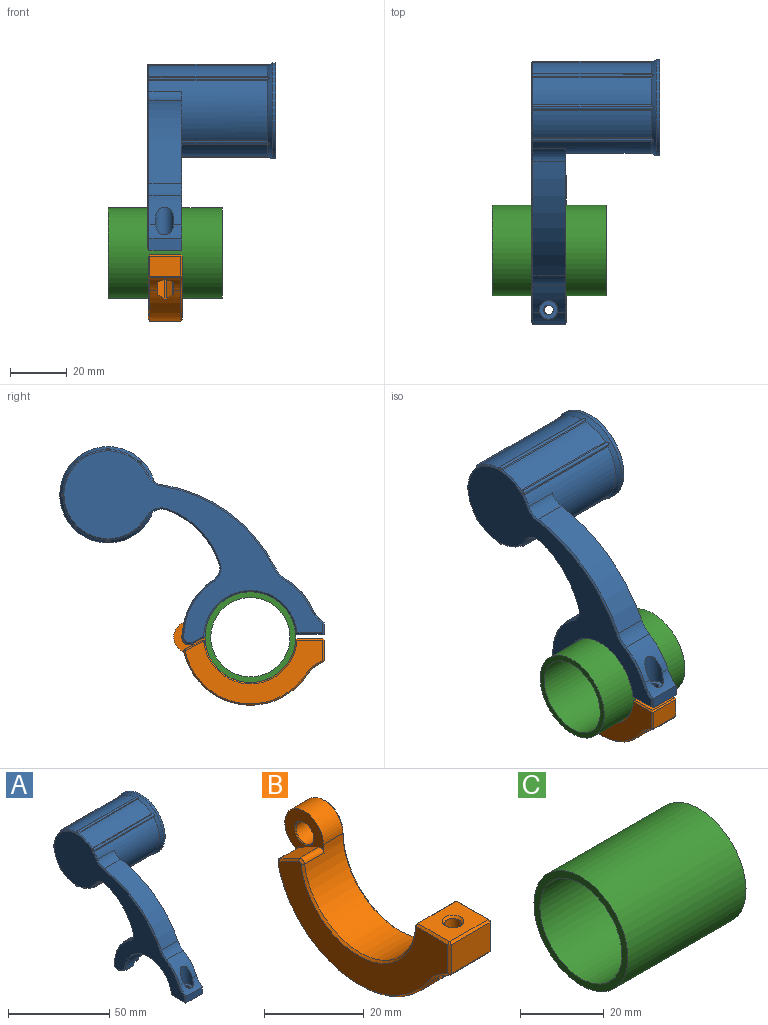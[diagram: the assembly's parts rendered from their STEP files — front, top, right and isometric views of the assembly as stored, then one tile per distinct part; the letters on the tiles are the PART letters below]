
ASSEMBLY  parts=3 mates=3
PART A: 98 faces, bbox 45x92.8x69.4 mm
  f0: cone r=15.9mm half-angle=30deg, axis (1,0,0), area 198.8mm2, adj f1,f2,f3,f4,f5,f6,f11,f26
  f1: cylinder r=15.9mm len=41.5mm, axis (-1,0,0), area 776.9mm2, adj f0,f20,f39,f40,f41,f54,f67,f97
  f2: cylinder r=15.9mm len=41.5mm, axis (-1,0,0), area 438.1mm2, adj f0,f42,f43,f90
  f3: cylinder r=15.9mm len=41.5mm, axis (-1,0,0), area 438.1mm2, adj f0,f44,f45,f82
  f4: cylinder r=15.9mm len=41.5mm, axis (-1,0,0), area 438.1mm2, adj f0,f46,f47,f74
  f5: cylinder r=15.9mm len=41.5mm, axis (-1,0,0), area 438.1mm2, adj f0,f48,f49,f66
  f6: cylinder r=15.9mm len=41.5mm, axis (-1,0,0), area 438.1mm2, adj f0,f50,f51,f58
  f7: cylinder r=23.9mm len=20.02mm, axis (-1,0,0), area 230.5mm2, adj f19,f20,f24,f36,f37,f89
  f8: cylinder r=15.9mm len=31.77mm, axis (-1,0,0), area 538mm2, adj f9,f18,f20,f24,f38,f83
  f9: plane 5.5x4.36mm, normal (0,-0.45,-0.89), area 26.9mm2, adj f8,f19,f24,f85
  f10: plane 5x5mm, normal (1,0,0), area 19.6mm2, adj f19
  f11: cylinder r=15.9mm len=41.5mm, axis (-1,0,0), area 438.1mm2, adj f0,f52,f53,f59
  f12: plane 91.27x67.9mm, normal (-1,0,0), area 1714.1mm2, adj f55,f56,f57,f58,f59,f60,f61,f62
  f13: cylinder r=30mm len=18.73mm, axis (-1,0,0), area 309mm2, adj f20,f36,f39,f93
  f14: cylinder r=54mm len=39.91mm, axis (-1,0,0), area 590.2mm2, adj f20,f35,f40,f71
  f15: cylinder r=23.9mm len=11.5mm, axis (-1,0,0), area 122.1mm2, adj f16,f20,f22,f35,f75
  f16: cylinder r=12mm len=11.5mm, axis (-1,0,0), area 54.5mm2, adj f15,f17,f20,f22,f77
  f17: plane 11.5x4mm, normal (0,-1,0), area 46mm2, adj f16,f18,f20,f79
  f18: plane 11.5x10mm, normal (0,0,-1), area 105.9mm2, adj f8,f17,f20,f21,f81
  f19: cylinder r=2.5mm len=11.5mm, axis (-1,0,0), area 122.3mm2, adj f7,f9,f10,f24,f87
  f20: plane 62.17x55.9mm, normal (1,0,0), area 1017.2mm2, adj f1,f7,f8,f13,f14,f15,f16,f17
  f21: cylinder r=1.7mm len=4mm, axis (0,0,-1), area 42.7mm2, adj f18,f23
  f22: cylinder r=3.25mm len=11.15mm, axis (0,0,-1), area 130.2mm2, adj f15,f16,f23
  f23: plane 6.5x6.5mm, normal (0,0,1), area 24.1mm2, adj f21,f22
  f24: plane 9.2x8.54mm, normal (1,0,0), area 32.8mm2, adj f7,f8,f9,f19,f25,f37,f38
  f25: cylinder r=5.7mm len=6mm, axis (1,0,0), area 32mm2, adj f20,f24,f37,f38
  f26: cylinder r=16.9mm len=33.8mm, axis (1,0,0), area 134.6mm2, adj f0,f27
  f27: plane 33.8x33.8mm, normal (1,0,0), area 897.3mm2, adj f26
  f28: cylinder r=0.7mm len=42.37mm, axis (-1,0,0), area 57.8mm2, adj f0,f53,f54,f63
  f29: cylinder r=0.7mm len=42.37mm, axis (-1,0,0), area 57.8mm2, adj f0,f51,f52,f55
  f30: cylinder r=0.7mm len=42.37mm, axis (-1,0,0), area 57.8mm2, adj f0,f49,f50,f62
  f31: cylinder r=0.7mm len=42.37mm, axis (-1,0,0), area 57.8mm2, adj f0,f47,f48,f70
  f32: cylinder r=0.7mm len=42.37mm, axis (-1,0,0), area 57.8mm2, adj f0,f45,f46,f78
  f33: cylinder r=0.7mm len=42.37mm, axis (-1,0,0), area 57.8mm2, adj f0,f43,f44,f86
  f34: cylinder r=0.7mm len=42.37mm, axis (-1,0,0), area 57.8mm2, adj f0,f41,f42,f94
  f35: cylinder r=10mm len=11.5mm, axis (1,0,0), area 64.1mm2, adj f14,f15,f20,f73
  f36: cylinder r=5mm len=11.5mm, axis (-1,0,0), area 75.4mm2, adj f7,f13,f20,f91
  f37: cylinder r=1mm len=6mm, axis (-1,0,0), area 11.7mm2, adj f7,f20,f24,f25
  f38: cylinder r=1mm len=6mm, axis (1,0,0), area 13mm2, adj f8,f20,f24,f25
  f39: cylinder r=6mm len=11.5mm, axis (-1,0,0), area 96.3mm2, adj f1,f13,f20,f95
  f40: cylinder r=6mm len=11.5mm, axis (1,0,0), area 66.7mm2, adj f1,f14,f20,f69
  f41: cylinder r=0.5mm len=41.85mm, axis (1,0,0), area 19.1mm2, adj f0,f1,f34,f96
  f42: cylinder r=0.5mm len=41.85mm, axis (1,0,0), area 19.1mm2, adj f0,f2,f34,f92
  f43: cylinder r=0.5mm len=41.85mm, axis (1,0,0), area 19.1mm2, adj f0,f2,f33,f88
  f44: cylinder r=0.5mm len=41.85mm, axis (1,0,0), area 19.1mm2, adj f0,f3,f33,f84
  f45: cylinder r=0.5mm len=41.85mm, axis (1,0,0), area 19.1mm2, adj f0,f3,f32,f80
  f46: cylinder r=0.5mm len=41.85mm, axis (1,0,0), area 19.1mm2, adj f0,f4,f32,f76
  f47: cylinder r=0.5mm len=41.85mm, axis (1,0,0), area 19.1mm2, adj f0,f4,f31,f72
  f48: cylinder r=0.5mm len=41.85mm, axis (1,0,0), area 19.1mm2, adj f0,f5,f31,f68
  f49: cylinder r=0.5mm len=41.85mm, axis (1,0,0), area 19.1mm2, adj f0,f5,f30,f64
  f50: cylinder r=0.5mm len=41.85mm, axis (1,0,0), area 19.1mm2, adj f0,f6,f30,f60
  f51: cylinder r=0.5mm len=41.85mm, axis (1,0,0), area 19.1mm2, adj f0,f6,f29,f56
  f52: cylinder r=0.5mm len=41.85mm, axis (1,0,0), area 19.1mm2, adj f0,f11,f29,f57
  f53: cylinder r=0.5mm len=41.85mm, axis (1,0,0), area 19.1mm2, adj f0,f11,f28,f61
  f54: cylinder r=0.5mm len=41.85mm, axis (1,0,0), area 19.1mm2, adj f0,f1,f28,f65
  f55: cone r=0.2mm half-angle=45deg, axis (1,0,0), area 0.6mm2, adj f12,f29,f56,f57
  f56: cone r=1mm half-angle=45deg, axis (-1,0,0), area 0.5mm2, adj f12,f51,f55,f58
  f57: cone r=1mm half-angle=45deg, axis (-1,0,0), area 0.5mm2, adj f12,f52,f55,f59
  f58: cone r=15.9mm half-angle=45deg, axis (1,0,0), area 7.3mm2, adj f6,f12,f56,f60
  f59: cone r=15.9mm half-angle=45deg, axis (1,0,0), area 7.3mm2, adj f11,f12,f57,f61
  f60: cone r=1mm half-angle=45deg, axis (-1,0,0), area 0.5mm2, adj f12,f50,f58,f62
  f61: cone r=1mm half-angle=45deg, axis (-1,0,0), area 0.5mm2, adj f12,f53,f59,f63
  f62: cone r=0.2mm half-angle=45deg, axis (1,0,0), area 0.6mm2, adj f12,f30,f60,f64
  f63: cone r=0.2mm half-angle=45deg, axis (1,0,0), area 0.6mm2, adj f12,f28,f61,f65
  f64: cone r=1mm half-angle=45deg, axis (-1,0,0), area 0.5mm2, adj f12,f49,f62,f66
  f65: cone r=1mm half-angle=45deg, axis (-1,0,0), area 0.5mm2, adj f12,f54,f63,f67
  f66: cone r=15.9mm half-angle=45deg, axis (1,0,0), area 7.3mm2, adj f5,f12,f64,f68
  f67: cone r=15.9mm half-angle=45deg, axis (1,0,0), area 3.1mm2, adj f1,f12,f65,f69
  f68: cone r=1mm half-angle=45deg, axis (-1,0,0), area 0.5mm2, adj f12,f48,f66,f70
  f69: cone r=6.5mm half-angle=45deg, axis (-1,0,0), area 4.3mm2, adj f12,f40,f67,f71
  f70: cone r=0.2mm half-angle=45deg, axis (1,0,0), area 0.6mm2, adj f12,f31,f68,f72
  f71: cone r=54mm half-angle=45deg, axis (1,0,0), area 36.1mm2, adj f12,f14,f69,f73
  f72: cone r=1mm half-angle=45deg, axis (-1,0,0), area 0.5mm2, adj f12,f47,f70,f74
  f73: cone r=10.5mm half-angle=45deg, axis (-1,0,0), area 4mm2, adj f12,f35,f71,f75
  f74: cone r=15.9mm half-angle=45deg, axis (1,0,0), area 7.3mm2, adj f4,f12,f72,f76
  f75: cone r=23.9mm half-angle=45deg, axis (1,0,0), area 10mm2, adj f12,f15,f73,f77
  f76: cone r=1mm half-angle=45deg, axis (-1,0,0), area 0.5mm2, adj f12,f46,f74,f78
  f77: cone r=12.5mm half-angle=45deg, axis (-1,0,0), area 4.6mm2, adj f12,f16,f75,f79
  f78: cone r=0.2mm half-angle=45deg, axis (1,0,0), area 0.6mm2, adj f12,f32,f76,f80
  f79: plane 4x0.5mm, normal (-0.71,-0.71,0), area 2.6mm2, adj f12,f17,f77,f81
  f80: cone r=1mm half-angle=45deg, axis (-1,0,0), area 0.5mm2, adj f12,f45,f78,f82
  f81: plane 10.01x0.51mm, normal (-0.71,0,-0.71), area 6.7mm2, adj f12,f18,f79,f83
  f82: cone r=15.9mm half-angle=45deg, axis (1,0,0), area 7.3mm2, adj f3,f12,f80,f84
  f83: cone r=16.4mm half-angle=45deg, axis (-1,0,0), area 34.9mm2, adj f8,f12,f81,f85
  f84: cone r=1mm half-angle=45deg, axis (-1,0,0), area 0.5mm2, adj f12,f44,f82,f86
  f85: plane 4.59x2.54mm, normal (-0.71,-0.32,-0.63), area 3.4mm2, adj f9,f12,f83,f87
  f86: cone r=0.2mm half-angle=45deg, axis (1,0,0), area 0.6mm2, adj f12,f33,f84,f88
  f87: cone r=2.5mm half-angle=45deg, axis (1,0,0), area 3.2mm2, adj f12,f19,f85,f89
  f88: cone r=1mm half-angle=45deg, axis (-1,0,0), area 0.5mm2, adj f12,f43,f86,f90
  f89: cone r=23.9mm half-angle=45deg, axis (1,0,0), area 16.6mm2, adj f7,f12,f87,f91
  f90: cone r=15.9mm half-angle=45deg, axis (1,0,0), area 7.3mm2, adj f2,f12,f88,f92
  f91: cone r=5.5mm half-angle=45deg, axis (-1,0,0), area 4.9mm2, adj f12,f36,f89,f93
  f92: cone r=1mm half-angle=45deg, axis (-1,0,0), area 0.5mm2, adj f12,f42,f90,f94
  f93: cone r=30.5mm half-angle=45deg, axis (-1,0,0), area 19.2mm2, adj f12,f13,f91,f95
  f94: cone r=0.2mm half-angle=45deg, axis (1,0,0), area 0.6mm2, adj f12,f34,f92,f96
  f95: cone r=6.5mm half-angle=45deg, axis (-1,0,0), area 6.2mm2, adj f12,f39,f93,f97
  f96: cone r=1mm half-angle=45deg, axis (-1,0,0), area 0.5mm2, adj f12,f41,f94,f97
  f97: cone r=15.9mm half-angle=45deg, axis (1,0,0), area 2.1mm2, adj f1,f12,f95,f96
PART B: 54 faces, bbox 12.1x52.9x29.5 mm
  f0: cylinder r=15.9mm len=31.77mm, axis (-1,0,0), area 527.7mm2, adj f6,f17,f20,f21,f23,f24
  f1: plane 48.24x22.4mm, normal (-1,0,0), area 431.8mm2, adj f22,f23,f27,f31,f32,f36,f40,f41
  f2: plane 11x9.02mm, normal (0,0,1), area 84mm2, adj f24,f29,f32,f33,f45
  f3: plane 11x7.15mm, normal (0,-1,0), area 78.7mm2, adj f33,f38,f41,f44
  f4: cylinder r=12mm len=11mm, axis (-1,0,0), area 52.6mm2, adj f5,f11,f12,f13,f14,f39,f40,f44
  f5: cylinder r=23.9mm len=43.26mm, axis (-1,0,0), area 599.4mm2, adj f4,f9,f10,f12,f13,f19,f35,f36
  f6: cylinder r=5.5mm len=11mm, axis (-1,0,0), area 131.7mm2, adj f0,f17,f19,f26
  f7: cylinder r=2.52mm len=5.3mm, axis (-1,0,0), area 84.1mm2, adj f46,f47
  f8: plane 51.79x28.4mm, normal (1,0,0), area 474.7mm2, adj f21,f26,f29,f30,f35,f38,f39,f46
  f9: plane 10.64x2.47mm, normal (-0.5,-0.87,0), area 27.1mm2, adj f5,f15,f49,f50
  f10: plane 10.64x2.47mm, normal (0.5,-0.87,0), area 27.1mm2, adj f5,f15,f50,f51
  f11: plane 4.78x2.45mm, normal (-0.5,0.87,0), area 11.8mm2, adj f4,f15,f48,f53
  f12: plane 8.31x2.77mm, normal (-1,0,0), area 18.1mm2, adj f4,f5,f15,f48,f49
  f13: plane 8.31x2.77mm, normal (1,0,0), area 18.1mm2, adj f4,f5,f15,f51,f52
  f14: plane 4.78x2.45mm, normal (0.5,0.87,0), area 11.8mm2, adj f4,f15,f52,f53
  f15: plane 6.54x5.8mm, normal (0,0,-1), area 20mm2, adj f9,f10,f11,f12,f13,f14,f16,f48
  f16: cylinder r=1.7mm len=4.5mm, axis (0,0,-1), area 48.1mm2, adj f15,f45
  f17: plane 11.13x10.65mm, normal (-1,0,0), area 56.6mm2, adj f0,f6,f18,f19,f20,f47
  f18: plane 5.58x5.5mm, normal (0,0.46,0.89), area 34.5mm2, adj f17,f19,f20,f27
  f19: cylinder r=1mm len=11mm, axis (-1,0,0), area 7.7mm2, adj f5,f6,f17,f18,f30,f31
  f20: cylinder r=1mm len=5.5mm, axis (-1,0,0), area 10.6mm2, adj f0,f17,f18,f22
  f21: cone r=15.9mm half-angle=45deg, axis (1,0,0), area 35.2mm2, adj f0,f8,f25,f26
  f22: cone r=0.5mm half-angle=45deg, axis (1,0,0), area 1mm2, adj f1,f20,f23,f27
  f23: cone r=16.4mm half-angle=45deg, axis (-1,0,0), area 33.7mm2, adj f0,f1,f22,f28
  f24: plane 11x0.5mm, normal (0,0.69,0.73), area 7.5mm2, adj f0,f2,f25,f28
  f25: plane 0.5x0.5mm, normal (0.59,0.55,0.59), area 0.2mm2, adj f21,f24,f29
  f26: cone r=5mm half-angle=45deg, axis (-1,0,0), area 16.3mm2, adj f6,f8,f21,f30
  f27: plane 5.81x3.33mm, normal (-0.71,0.32,0.63), area 4.4mm2, adj f1,f18,f22,f31
  f28: plane 0.5x0.5mm, normal (-0.59,0.55,0.59), area 0.2mm2, adj f23,f24,f32
  f29: plane 9.02x0.5mm, normal (0.71,0,0.71), area 6.4mm2, adj f2,f8,f25,f34
  f30: cone r=0.5mm half-angle=45deg, axis (-1,0,0), area 0.2mm2, adj f8,f19,f26,f35
  f31: cone r=0.5mm half-angle=45deg, axis (1,0,0), area 0.7mm2, adj f1,f19,f27,f36
  f32: plane 9.02x0.5mm, normal (-0.71,0,0.71), area 6.4mm2, adj f1,f2,f28,f37
  f33: plane 11x0.5mm, normal (0,-0.71,0.71), area 7.8mm2, adj f2,f3,f34,f37
  f34: plane 0.5x0.5mm, normal (0.58,-0.58,0.58), area 0.2mm2, adj f29,f33,f38
  f35: cone r=23.4mm half-angle=45deg, axis (-1,0,0), area 39.1mm2, adj f5,f8,f30,f39
  f36: cone r=23.9mm half-angle=45deg, axis (1,0,0), area 39.1mm2, adj f1,f5,f31,f40
  f37: plane 0.5x0.5mm, normal (-0.58,-0.58,0.58), area 0.2mm2, adj f32,f33,f41
  f38: plane 7.15x0.5mm, normal (0.71,-0.71,0), area 5.1mm2, adj f3,f8,f34,f42
  f39: cone r=12mm half-angle=45deg, axis (1,0,0), area 5.3mm2, adj f4,f8,f35,f42
  f40: cone r=12.5mm half-angle=45deg, axis (-1,0,0), area 5.3mm2, adj f1,f4,f36,f43
  f41: plane 7.15x0.5mm, normal (-0.71,-0.71,0), area 5.1mm2, adj f1,f3,f37,f43
  f42: plane 0.5x0.5mm, normal (0.64,-0.64,-0.43), area 0.2mm2, adj f38,f39,f44
  f43: plane 0.5x0.5mm, normal (-0.64,-0.64,-0.43), area 0.2mm2, adj f40,f41,f44
  f44: plane 11x0.47mm, normal (0,-0.83,-0.56), area 6.2mm2, adj f3,f4,f42,f43
  f45: cone r=1.7mm half-angle=45deg, axis (0,0,1), area 8.7mm2, adj f2,f16
  f46: cone r=2.52mm half-angle=45deg, axis (1,0,0), area 12.3mm2, adj f7,f8
  f47: cone r=2.73mm half-angle=45deg, axis (-1,0,0), area 4.7mm2, adj f7,f17
  f48: cylinder r=0.5mm len=5.07mm, axis (0,0,-1), area 2.6mm2, adj f4,f11,f12,f15
  f49: cylinder r=0.5mm len=8.9mm, axis (0,0,-1), area 4.5mm2, adj f5,f9,f12,f15
  f50: cylinder r=0.5mm len=10.65mm, axis (0,0,-1), area 5.6mm2, adj f5,f9,f10,f15
  f51: cylinder r=0.5mm len=8.9mm, axis (0,0,-1), area 4.5mm2, adj f5,f10,f13,f15
  f52: cylinder r=0.5mm len=5.07mm, axis (0,0,-1), area 2.6mm2, adj f4,f13,f14,f15
  f53: cylinder r=0.5mm len=3.82mm, axis (0,0,-1), area 2mm2, adj f4,f11,f14,f15
PART C: 4 faces, bbox 40x31.8x31.8 mm
  f0: cylinder r=13.9mm len=40mm, axis (-1,0,0), area 3493.5mm2, adj f2,f3
  f1: cylinder r=15.9mm len=40mm, axis (-1,0,0), area 3996.1mm2, adj f2,f3
  f2: plane 31.8x31.8mm, normal (1,0,0), area 187.2mm2, adj f0,f1
  f3: plane 31.8x31.8mm, normal (-1,0,0), area 187.2mm2, adj f0,f1
PLACE A t=(0.02,0.11,-0.07)mm
PLACE B t=(0.27,0.11,-0.07)mm
PLACE C t=(-19.73,0.11,-0.07)mm fixed
MATE cylindrical B.f7 <-> A.f19  axis (-1,0,0) through (3.12,21.51,-0.07)mm
MATE revolute A.f8 <-> C.f1  axis (-1,0,0) through (0.27,0.11,-0.07)mm
MATE revolute B.f0 <-> C.f1  axis (-1,0,0) through (0.27,0.11,-0.07)mm
